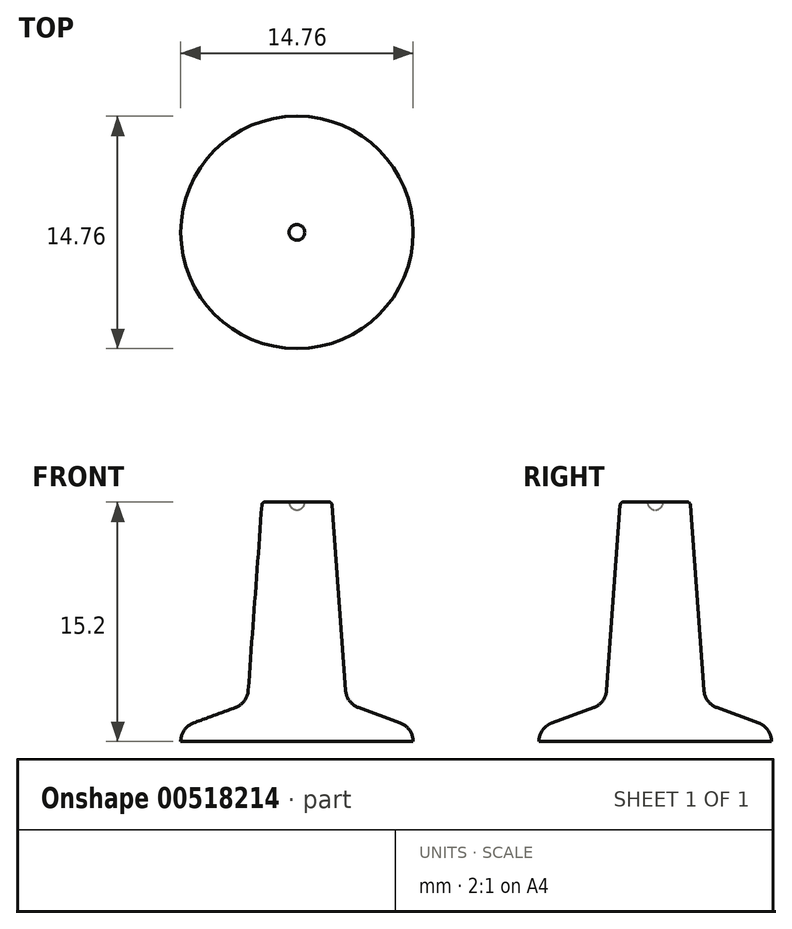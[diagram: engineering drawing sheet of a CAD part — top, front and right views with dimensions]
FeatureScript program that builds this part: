
annotation { "Feature Type Name" : "Feature", "Feature Type Description" : "" }
export const myFeature = defineFeature(function(context is Context, id is Id, definition is map)
    precondition{}
    {
        {
            var Q0;
            Q0=qCreatedBy(makeId("Front.planeOp"),FACE);
            var sketch = newSketch(context, id + "F0", { "sketchPlane" : qUnion([Q0])});
            skLineSegment(sketch, "E0", {"start": v(0, 0) * mm, "end": v(7.38, 0) * mm});
            skLineSegment(sketch, "E1", {"start": v(0, 0) * mm, "end": v(0, 14.7) * mm});
            skLineSegment(sketch, "E2", {"start": v(0.5, 15.2) * mm, "end": v(2.03, 15.2) * mm});
            skLineSegment(sketch, "E3", {"start": v(3.1, 3.23) * mm, "end": v(2.23, 15.01) * mm});
            skArc(sketch, "E4", {"start": v(7.38, 0) * mm, "mid": v(7.15, 0.72) * mm, "end": v(6.56, 1.17) * mm});
            skLineSegment(sketch, "E5", {"start": v(6.56, 1.17) * mm, "end": v(3.9, 2.15) * mm});
            skPoint(sketch, "E6.visualSharp", {"position": v(3.15, 2.42) * mm});
            skArc(sketch, "E6.filletArc", {"start": v(3.1, 3.23) * mm, "mid": v(3.34, 2.57) * mm, "end": v(3.9, 2.15) * mm});
            skArc(sketch, "E7", {"start": v(0, 14.7) * mm, "mid": v(0.35, 14.85) * mm, "end": v(0.5, 15.2) * mm});
            skPoint(sketch, "E8.visualSharp", {"position": v(2.21, 15.2) * mm});
            skArc(sketch, "E8.filletArc", {"start": v(2.23, 15.01) * mm, "mid": v(2.17, 15.15) * mm, "end": v(2.03, 15.2) * mm});
            skSolve(sketch);
        }
        {
            var Q0;
            Q0=makeQuery(id+"F0.imprint","IMPRINT",FACE,{"disambiguationData":[TD([[makeQuery(id+"F0.imprint","IMPRINT",EDGE,{"derivedFrom":sQuery(id+"F0.wireOp",EDGE,"E0")}),1.0]])]});
            var Q1;
            Q1=sQuery(id+"F0.wireOp",EDGE,"E1");
            revolve(context, id + "F1", {"entities" : qUnion([Q0]), "axis" : qUnion([Q1]), "revolveType" : RevolveType.FULL});
        }
    });
